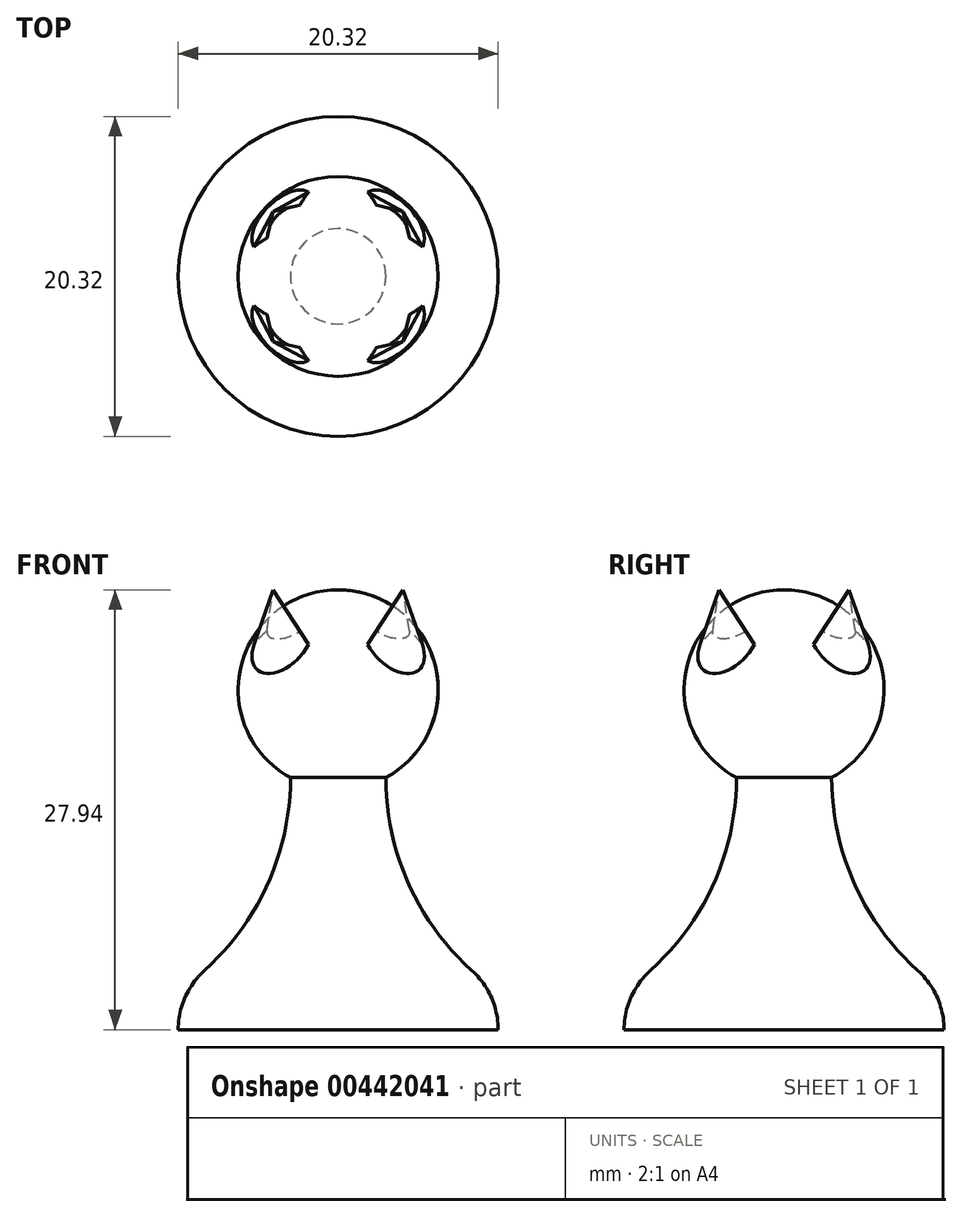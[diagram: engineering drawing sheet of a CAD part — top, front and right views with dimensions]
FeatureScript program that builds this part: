
annotation { "Feature Type Name" : "Feature", "Feature Type Description" : "" }
export const myFeature = defineFeature(function(context is Context, id is Id, definition is map)
    precondition{}
    {
        {
            var Q0;
            Q0=qCreatedBy(makeId("Front.planeOp"),FACE);
            var sketch = newSketch(context, id + "F0", { "sketchPlane" : qUnion([Q0])});
            skArc(sketch, "E0", {"start": v(0, 27.94) * mm, "mid": v(-6.35, 21.6) * mm, "end": v(0, 15.24) * mm});
            skLineSegment(sketch, "E1", {"start": v(0, 0) * mm, "end": v(-10.16, 0) * mm});
            skArc(sketch, "E2", {"start": v(-8.48, 3.77) * mm, "mid": v(-9.72, 2.07) * mm, "end": v(-10.16, 0) * mm});
            skArc(sketch, "E3", {"start": v(-8.48, 3.77) * mm, "mid": v(-4.45, 9.31) * mm, "end": v(-3.02, 16) * mm});
            skLineSegment(sketch, "E4", {"start": v(-3.02, 16) * mm, "end": v(-3.02, 0) * mm, "construction": true});
            skLineSegment(sketch, "E5", {"start": v(0, 27.94) * mm, "end": v(0, 0) * mm});
            skLineSegment(sketch, "E6", {"start": v(-10.16, 0) * mm, "end": v(-10.16, 3.2) * mm, "construction": true});
            skPoint(sketch, "E7", {"position": v(-6.35, 21.6) * mm});
            skSolve(sketch);
        }
        {
            var Q0;
            Q0 = qSketchRegion(id + "F0", true);
            var Q1;
            Q1=sQuery(id+"F0.wireOp",EDGE,"E5");
            revolve(context, id + "F1", {"entities" : qUnion([Q0]), "axis" : qUnion([Q1]), "revolveType" : RevolveType.FULL});
        }
        {
            var Q0;
            Q0=qCreatedBy(makeId("Top.planeOp"),FACE);
            cPlane(context, id + "F2", {"entities" : qUnion([Q0]), "cplaneType" : CPlaneType.OFFSET, "offset" : 21.59 * mm, "width" : 152.4 * mm, "height" : 152.4 * mm});
        }
        {
            var Q0;
            Q0=qCreatedBy(id+"F2.planeOp",FACE);
            var sketch = newSketch(context, id + "F3", { "sketchPlane" : qUnion([Q0])});
            skCircle(sketch, "E8", {"center": v(0, 0) * mm, "radius": 6.35 * mm});
            skCircle(sketch, "E9.0", {"center": v(0, 0) * mm, "radius": 5.08 * mm});
            skLineSegment(sketch, "E10", {"start": v(0, 6.35) * mm, "end": v(0, 5.08) * mm});
            skLineSegment(sketch, "E11", {"start": v(5.08, 0) * mm, "end": v(6.35, 0) * mm});
            skLineSegment(sketch, "E12", {"start": v(0, -6.35) * mm, "end": v(0, -5.08) * mm});
            skLineSegment(sketch, "E13", {"start": v(-6.35, 0) * mm, "end": v(-5.08, 0) * mm});
            skSolve(sketch);
        }
        {
            var Q0;
            Q0=qCreatedBy(makeId("Top.planeOp"),FACE);
            cPlane(context, id + "F4", {"entities" : qUnion([Q0]), "cplaneType" : CPlaneType.OFFSET, "offset" : 27.94 * mm, "width" : 152.4 * mm, "height" : 152.4 * mm});
        }
        {
            var Q0;
            Q0=qCreatedBy(id+"F4.planeOp",FACE);
            var sketch = newSketch(context, id + "F5", { "sketchPlane" : qUnion([Q0])});
            skCircle(sketch, "E14.cCircle", {"center": v(0, 0) * mm, "radius": 4.13 * mm, "construction": true});
            skLineSegment(sketch, "E14.0", {"start": v(4.13, 4.13) * mm, "end": v(4.13, -4.13) * mm});
            skLineSegment(sketch, "E14.1", {"start": v(4.13, -4.13) * mm, "end": v(-4.13, -4.13) * mm});
            skLineSegment(sketch, "E14.2", {"start": v(-4.13, -4.13) * mm, "end": v(-4.13, 4.13) * mm});
            skLineSegment(sketch, "E14.3", {"start": v(-4.13, 4.13) * mm, "end": v(4.13, 4.13) * mm});
            skPoint(sketch, "E14.0.midPoint", {"position": v(4.13, 0) * mm});
            skSolve(sketch);
        }
        {
            var Q0;
            {var subQ0=sQuery(id+"F3.wireOp",EDGE,"E12");Q0=makeQuery(id+"F3.imprint","IMPRINT",FACE,{"disambiguationData":[TD([[makeQuery(id+"F3.imprint","IMPRINT",EDGE,{"derivedFrom":subQ0}),1.0]])]});}
            var Q1;
            Q1=sQuery(id+"F5.wireOp",VERTEX,"E14.2.start");
            loft(context, id + "F6", {"operationType" : NewBodyOperationType.ADD, "sheetProfilesArray" : [{ "sheetProfileEntities" : qUnion([Q0]) }, { "sheetProfileEntities" : qUnion([Q1]) }]});
        }
        {
            var Q0;
            {var subQ0=sQuery(id+"F3.wireOp",EDGE,"E10");Q0=makeQuery(id+"F3.imprint","IMPRINT",FACE,{"disambiguationData":[TD([[makeQuery(id+"F3.imprint","IMPRINT",EDGE,{"derivedFrom":subQ0}),-1.0]])]});}
            var Q1;
            Q1=sQuery(id+"F5.wireOp",VERTEX,"E14.3.start");
            loft(context, id + "F7", {"operationType" : NewBodyOperationType.ADD, "sheetProfilesArray" : [{ "sheetProfileEntities" : qUnion([Q0]) }, { "sheetProfileEntities" : qUnion([Q1]) }]});
        }
        {
            var Q0;
            {var subQ0=sQuery(id+"F3.wireOp",EDGE,"E10");Q0=makeQuery(id+"F3.imprint","IMPRINT",FACE,{"disambiguationData":[TD([[makeQuery(id+"F3.imprint","IMPRINT",EDGE,{"derivedFrom":subQ0}),1.0]])]});}
            var Q1;
            Q1=sQuery(id+"F5.wireOp",VERTEX,"E14.0.start");
            loft(context, id + "F8", {"operationType" : NewBodyOperationType.ADD, "sheetProfilesArray" : [{ "sheetProfileEntities" : qUnion([Q0]) }, { "sheetProfileEntities" : qUnion([Q1]) }]});
        }
        {
            var Q0;
            {var subQ0=sQuery(id+"F3.wireOp",EDGE,"E11");Q0=makeQuery(id+"F3.imprint","IMPRINT",FACE,{"disambiguationData":[TD([[makeQuery(id+"F3.imprint","IMPRINT",EDGE,{"derivedFrom":subQ0}),-1.0]])]});}
            var Q1;
            Q1=sQuery(id+"F5.wireOp",VERTEX,"E14.1.start");
            loft(context, id + "F9", {"operationType" : NewBodyOperationType.ADD, "sheetProfilesArray" : [{ "sheetProfileEntities" : qUnion([Q0]) }, { "sheetProfileEntities" : qUnion([Q1]) }]});
        }
    });
